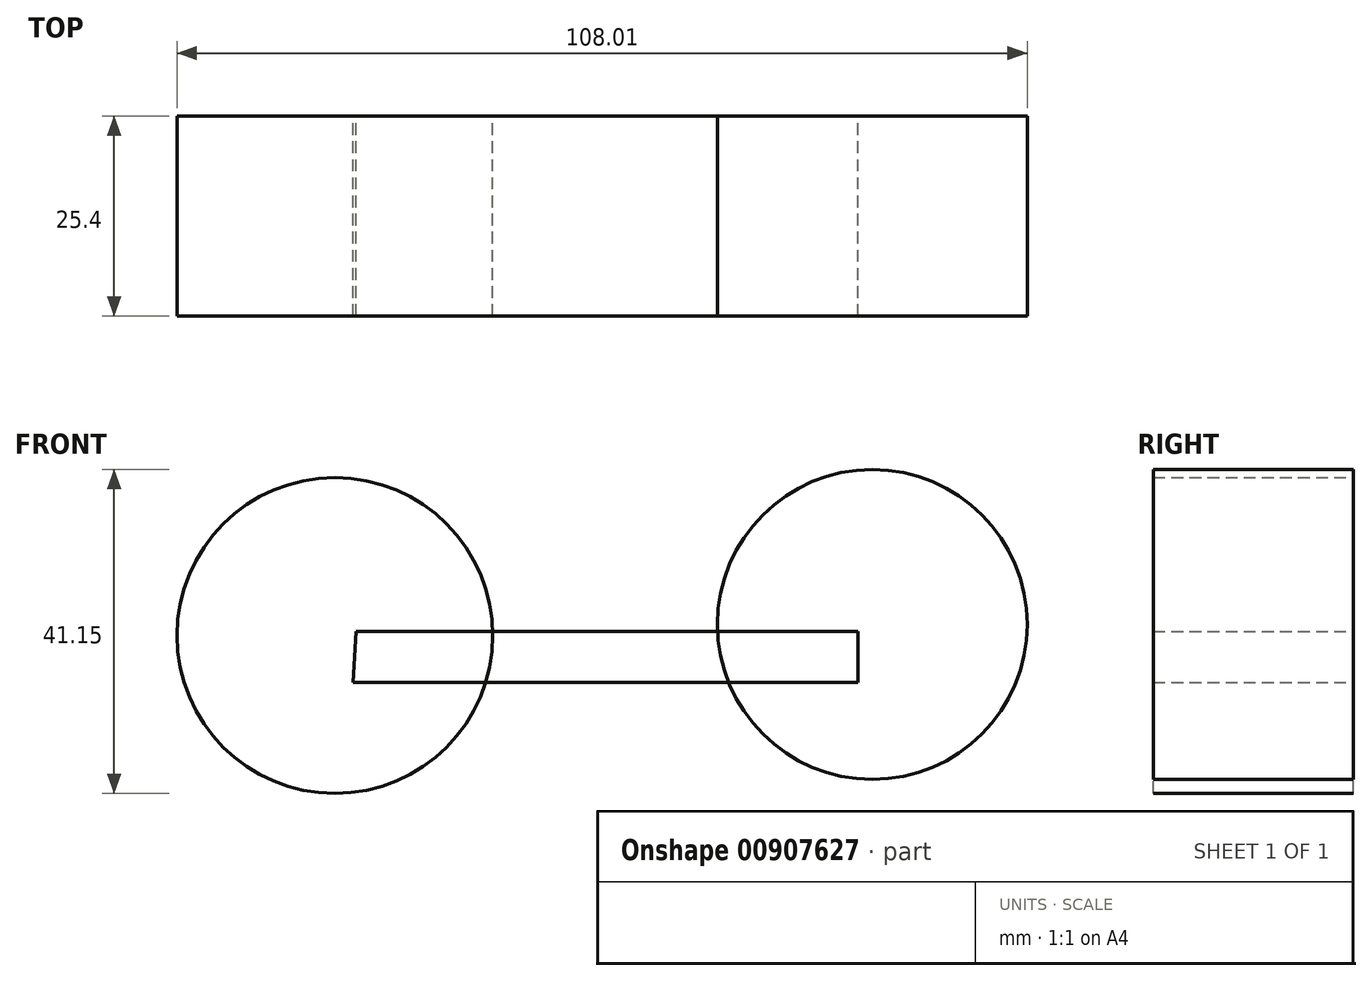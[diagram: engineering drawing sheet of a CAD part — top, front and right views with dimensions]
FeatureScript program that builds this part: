
annotation { "Feature Type Name" : "Feature", "Feature Type Description" : "" }
export const myFeature = defineFeature(function(context is Context, id is Id, definition is map)
    precondition{}
    {
        {
            var Q0;
            Q0=qCreatedBy(makeId("Front.planeOp"),FACE);
            var sketch = newSketch(context, id + "F0", { "sketchPlane" : qUnion([Q0])});
            skCircle(sketch, "E0", {"center": v(-38.9, 13.23) * mm, "radius": 20.05 * mm});
            skPoint(sketch, "E0.first.point", {"position": v(-50.24, 29.77) * mm});
            skPoint(sketch, "E0.second.point", {"position": v(-30.7, -5.07) * mm});
            skPoint(sketch, "E0.third.point", {"position": v(-54.3, 26.09) * mm});
            skCircle(sketch, "E1", {"center": v(29.37, 14.64) * mm, "radius": 19.68 * mm});
            skPoint(sketch, "E1.first.point", {"position": v(36.78, -3.6) * mm});
            skPoint(sketch, "E1.second.point", {"position": v(15.76, 28.85) * mm});
            skPoint(sketch, "E1.third.point", {"position": v(13.37, 26.09) * mm});
            skSolve(sketch);
        }
        {
            var Q0;
            Q0 = qSketchRegion(id + "F0", true);
            extrude(context, id + "F1", {"entities" : qUnion([Q0]), "depth" : 25.4 * mm, "offsetDistance" : 25.4 * mm});
        }
        {
            var Q0;
            Q0=qCreatedBy(makeId("Front.planeOp"),FACE);
            var sketch = newSketch(context, id + "F2", { "sketchPlane" : qUnion([Q0])});
            skLineSegment(sketch, "E2", {"start": v(-36.23, 13.73) * mm, "end": v(27.56, 13.73) * mm});
            skLineSegment(sketch, "E3", {"start": v(27.56, 13.73) * mm, "end": v(27.56, 7.28) * mm});
            skLineSegment(sketch, "E4", {"start": v(27.56, 7.28) * mm, "end": v(-36.6, 7.28) * mm});
            skLineSegment(sketch, "E5", {"start": v(-36.6, 7.28) * mm, "end": v(-36.23, 13.73) * mm});
            skSolve(sketch);
        }
        {
            var Q0;
            Q0=makeQuery(id+"F2.imprint","IMPRINT",FACE,{"disambiguationData":[TD([[makeQuery(id+"F2.imprint","IMPRINT",EDGE,{"derivedFrom":sQuery(id+"F2.wireOp",EDGE,"E2")}),-1.0]])]});
            extrude(context, id + "F3", {"entities" : qUnion([Q0]), "depth" : 25.4 * mm, "offsetDistance" : 25.4 * mm});
        }
    });
